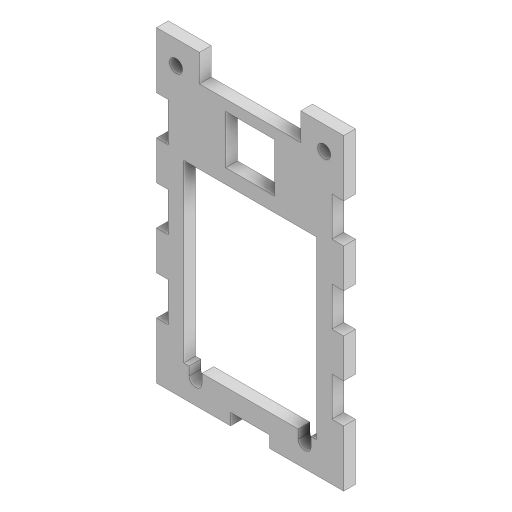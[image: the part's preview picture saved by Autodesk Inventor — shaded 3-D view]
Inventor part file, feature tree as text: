
AUTODESK INVENTOR PART (.ipt)
format: ipt  version: 2023.3 (Build 273359000, 359)  size: 189,952 bytes
history: native  units: mm
features: extrude x1, sketch x1
ambient origin geometry x8: Origin, YZ Plane, XZ Plane, XY Plane, X Axis, Y Axis, Z Axis, Center Point
bodies: Solid1 (feature_tree)
feature tree (2):
  extrude  "Extrusion1"  Depth=3.3mm
  sketch  "Sketch1"  dims[d0=3.3mm d1=3.3mm d2=28.0mm d3=14.0mm d4=3.3mm d5=3.3mm d6=38.0mm d7=19.0mm d8=34.0mm d9=44.0mm d10=3.25mm d11=20.0mm d12=5.0mm d13=10.0mm d14=9.0mm d15=26.0mm d16=7.0mm d17=1.0mm d18=3.0mm d19=10.0mm d20=10.0mm d21=3.0mm d22=10.0mm d23=3.0mm d24=20.0mm d26=20.0mm d27=10.0mm d29=10.0mm d31=20.0mm d33=20.0mm d34=10.0mm d36=10.0mm d38=3.0mm d39=10.0mm d40=20.0mm d42=20.0mm d43=10.0mm d45=10.0mm d47=20.0mm d49=20.0mm d50=10.0mm d52=10.0mm d54=3.0mm d55=0.0mm d56=12.5mm d57=12.5mm d58=7.0mm d59=26.0mm]
